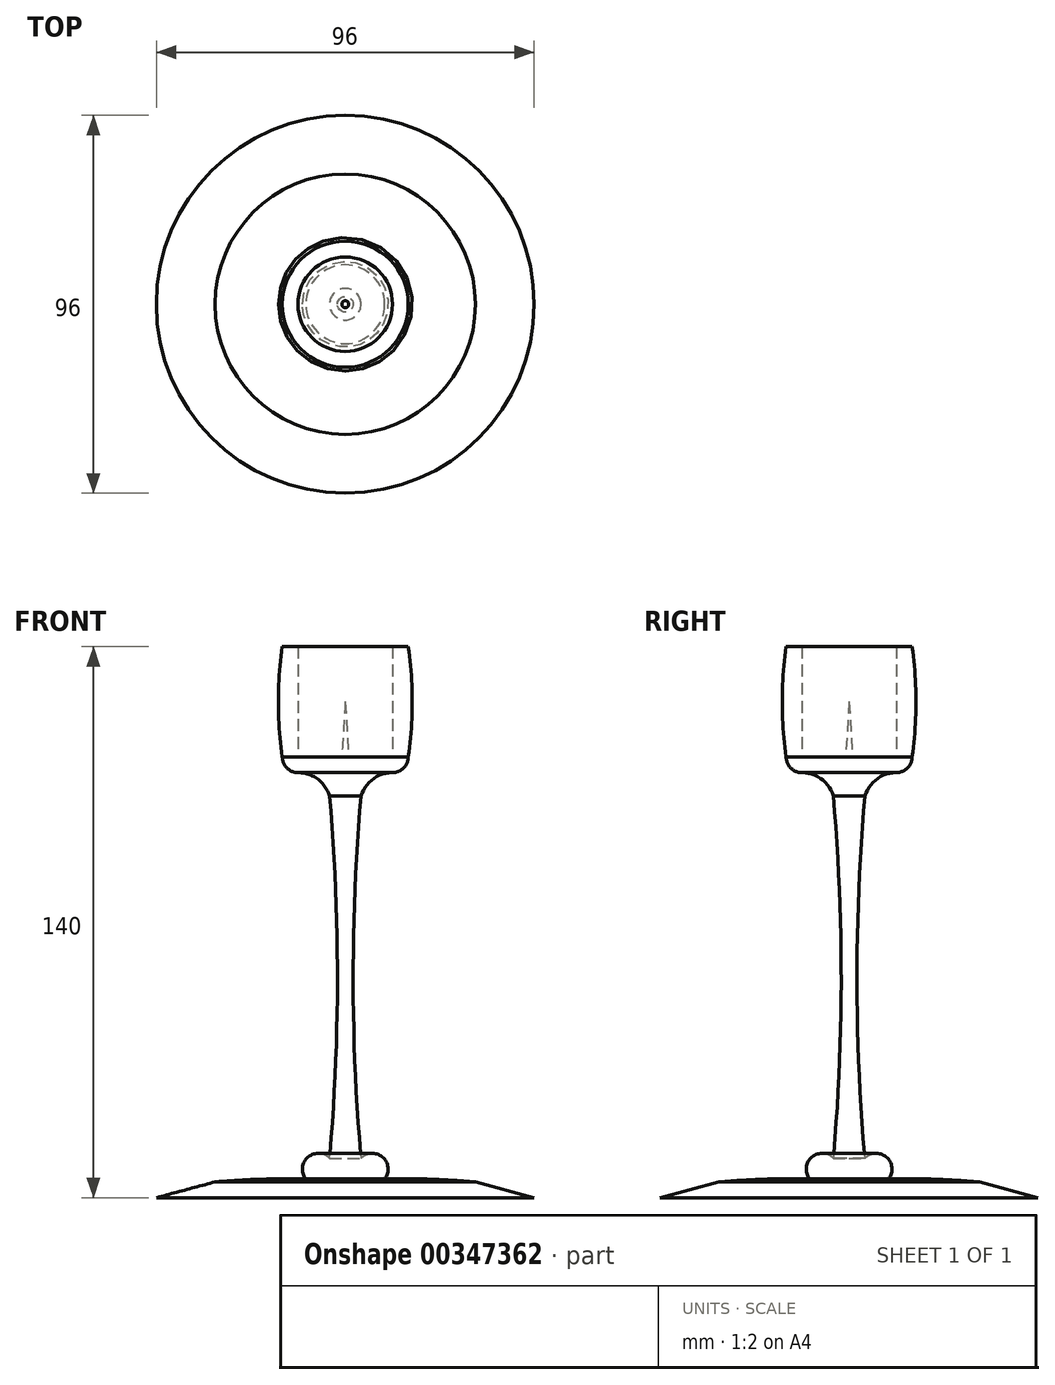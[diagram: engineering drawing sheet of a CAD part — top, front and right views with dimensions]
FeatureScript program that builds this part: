
annotation { "Feature Type Name" : "Feature", "Feature Type Description" : "" }
export const myFeature = defineFeature(function(context is Context, id is Id, definition is map)
    precondition{}
    {
        {
            var Q0;
            Q0=qCreatedBy(makeId("Front.planeOp"),FACE);
            var sketch = newSketch(context, id + "F0", { "sketchPlane" : qUnion([Q0])});
            skLineSegment(sketch, "E0", {"start": v(0, 0) * mm, "end": v(-48, 0) * mm});
            skLineSegment(sketch, "E1", {"start": v(0, 0) * mm, "end": v(0, 112) * mm});
            skLineSegment(sketch, "E2", {"start": v(0, 112) * mm, "end": v(-12, 112) * mm});
            skLineSegment(sketch, "E3", {"start": v(-12, 112) * mm, "end": v(-12, 140) * mm});
            skLineSegment(sketch, "E4", {"start": v(-12, 140) * mm, "end": v(-16, 140) * mm});
            skLineSegment(sketch, "E5", {"start": v(-12, 112) * mm, "end": v(-16, 112) * mm, "construction": true});
            skLineSegment(sketch, "E6", {"start": v(-12, 112) * mm, "end": v(-12, 108) * mm, "construction": true});
            skLineSegment(sketch, "E7", {"start": v(0, 102) * mm, "end": v(-4, 102) * mm, "construction": true});
            skLineSegment(sketch, "E8", {"start": v(0, 10) * mm, "end": v(-4, 10) * mm, "construction": true});
            skArc(sketch, "E9", {"start": v(-4, 10) * mm, "mid": v(-2, 56) * mm, "end": v(-4, 102) * mm});
            skArc(sketch, "E10", {"start": v(-4, 102) * mm, "mid": v(-7, 106.34) * mm, "end": v(-12, 108) * mm});
            skArc(sketch, "E11", {"start": v(-16, 112) * mm, "mid": v(-14.83, 109.17) * mm, "end": v(-12, 108) * mm});
            skArc(sketch, "E12", {"start": v(-16, 140) * mm, "mid": v(-17, 126) * mm, "end": v(-16, 112) * mm});
            skArc(sketch, "E13", {"start": v(-4, 10) * mm, "mid": v(-9.53, 10.24) * mm, "end": v(-10, 4.72) * mm});
            skArc(sketch, "E14", {"start": v(-10, 4.72) * mm, "mid": v(-21.55, 4.7) * mm, "end": v(-33.07, 4) * mm});
            skPoint(sketch, "E15.orphan", {"position": v(-4, 4.47) * mm});
            skLineSegment(sketch, "E16", {"start": v(0, 112) * mm, "end": v(0, 126) * mm});
            skLineSegment(sketch, "E17", {"start": v(0, 126) * mm, "end": v(-0.88, 112) * mm});
            skLineSegment(sketch, "E18", {"start": v(-48, 0) * mm, "end": v(-33.07, 4) * mm});
            skLineSegment(sketch, "E19", {"start": v(-33.07, 4) * mm, "end": v(-33.07, 0) * mm, "construction": true});
            skSolve(sketch);
        }
        {
            var Q0;
            Q0 = qSketchRegion(id + "F0", true);
            var Q1;
            Q1=sQuery(id+"F0.wireOp",EDGE,"E1");
            revolve(context, id + "F1", {"entities" : qUnion([Q0]), "axis" : qUnion([Q1]), "revolveType" : RevolveType.FULL});
        }
    });
